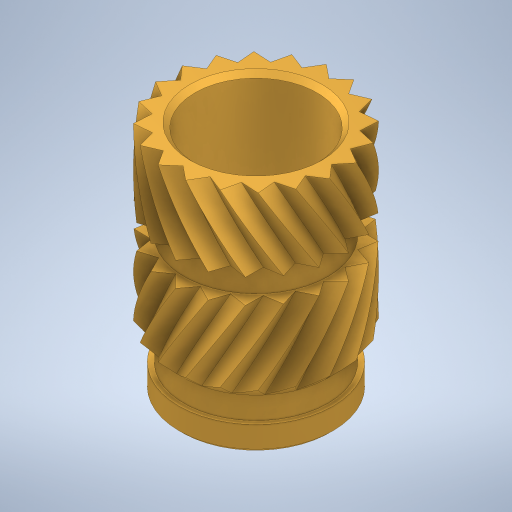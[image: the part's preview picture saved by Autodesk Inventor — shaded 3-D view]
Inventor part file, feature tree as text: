
AUTODESK INVENTOR PART (.ipt)
format: ipt  version: 2024 (Build 280153000, 153)  size: 576,512 bytes
history: native  units: mm
features: chamfer x2, sketch x2, revolve x1, plane x1, helix x1, pattern_circular x1, mirror x1
ambient origin geometry x8: Origin, YZ Plane, XZ Plane, XY Plane, X Axis, Y Axis, Z Axis, Center Point
bodies: Solid1 (feature_tree)
feature tree (9):
  revolve  "Revolution1"  [1 undecoded]
  chamfer  "Chamfer1"  Distance=0.4mm
  plane  "Work Plane1"
  helix  "Coil1"  [1 undecoded]
  pattern_circular  "Circular Pattern1"  [2 undecoded]
  mirror  "Mirror1"
  chamfer  "Chamfer2"  Distance=3.0mm
  sketch  "Sketch1"  dims[d0=7.1mm d1=9.5mm]
  sketch  "Sketch2"  dims[d2=0.6mm d4=0.4mm d5=45.0deg d6=1.0mm d7=3.0mm d8=1.0mm d9=2.5mm d10=90.0deg d11=0.125mm d12=2.0mm d13=45.0deg d14=3.141593mm d15=17.453293mm d16=3.0mm d17=4.5mm d18=1.25mm d19=0.0mm d20=45.0deg d21=1.745329mm d22=0.0mm d23=0.0mm d24=200.0mm d25=360.0deg d27=0.2mm d28=2.0mm d29=45.0deg]
note: 4 required parameter values undecoded (feature->parameter linkage not recoverable at this tier; creation-order binding heuristic only, values carry confidence <= 0.55)